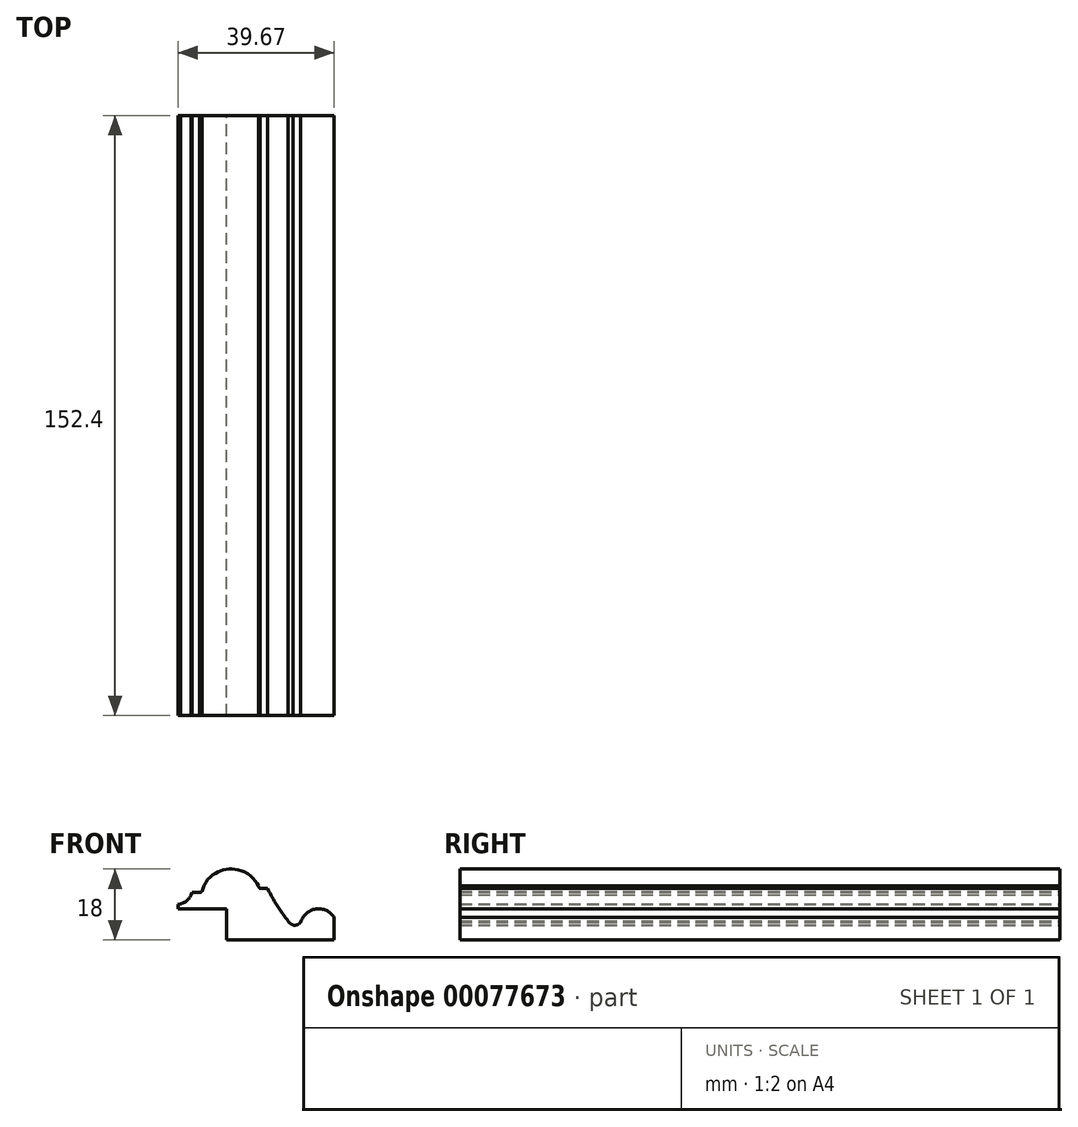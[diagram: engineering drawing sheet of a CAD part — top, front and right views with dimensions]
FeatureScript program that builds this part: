
annotation { "Feature Type Name" : "Feature", "Feature Type Description" : "" }
export const myFeature = defineFeature(function(context is Context, id is Id, definition is map)
    precondition{}
    {
        {
            var Q0;
            Q0=qCreatedBy(makeId("Front.planeOp"),FACE);
            var sketch = newSketch(context, id + "F0", { "sketchPlane" : qUnion([Q0])});
            skLineSegment(sketch, "E0", {"start": v(19.8, -3.3) * mm, "end": v(19.8, -8.99) * mm});
            skLineSegment(sketch, "E1", {"start": v(19.8, -8.99) * mm, "end": v(-7.51, -8.99) * mm});
            skLineSegment(sketch, "E2", {"start": v(-7.51, -8.99) * mm, "end": v(-7.51, -1.08) * mm});
            skLineSegment(sketch, "E3", {"start": v(-7.51, -1.08) * mm, "end": v(-19.86, -1.08) * mm});
            skLineSegment(sketch, "E4", {"start": v(-19.86, -1.08) * mm, "end": v(-19.86, 0) * mm});
            skArc(sketch, "E5", {"start": v(-16.55, 2.43) * mm, "mid": v(-17.63, 0.97) * mm, "end": v(-19.24, 0.14) * mm});
            skArc(sketch, "E6", {"start": v(11.31, -4.54) * mm, "mid": v(15.16, -1.16) * mm, "end": v(19.8, -3.3) * mm});
            skArc(sketch, "E7", {"start": v(11.31, -4.54) * mm, "mid": v(10.68, -5.03) * mm, "end": v(9.9, -5.25) * mm});
            skArc(sketch, "E8", {"start": v(9.9, -5.25) * mm, "mid": v(9.65, -5.26) * mm, "end": v(9.4, -5.24) * mm});
            skArc(sketch, "E9", {"start": v(9.4, -5.24) * mm, "mid": v(8.65, -4.83) * mm, "end": v(8.07, -4.2) * mm});
            skFitSpline(sketch, "E10", {"points": [v(8.07, -4.2) * mm, v(5.46, -0.55) * mm, v(3.74, 2.39) * mm, v(2.9, 4.04) * mm], "startDerivative": vector(-6.87, 9.23) * mm, "endDerivative": vector(-2.98, 6.05) * mm});
            skLineSegment(sketch, "E11", {"start": v(2.9, 4.04) * mm, "end": v(0.99, 4.04) * mm});
            skArc(sketch, "E12", {"start": v(0.99, 4.04) * mm, "mid": v(0.7, 4.33) * mm, "end": v(0.53, 4.7) * mm});
            skArc(sketch, "E13", {"start": v(-13.83, 3.33) * mm, "mid": v(-14.05, 3.12) * mm, "end": v(-14.35, 3.03) * mm});
            skLineSegment(sketch, "E14", {"start": v(-14.35, 3.03) * mm, "end": v(-16.35, 3.03) * mm});
            skLineSegment(sketch, "E15", {"start": v(-16.35, 3.03) * mm, "end": v(-16.55, 2.43) * mm});
            skFitSpline(sketch, "E16", {"points": [v(-13.83, 3.33) * mm, v(-12.94, 5.39) * mm, v(-11.55, 7.11) * mm, v(-9.76, 8.23) * mm, v(-8.4, 8.75) * mm, v(-6.54, 9) * mm, v(-4.7, 8.84) * mm, v(-2.28, 7.88) * mm, v(-0.46, 6.18) * mm, v(0.53, 4.7) * mm], "startDerivative": vector(6.84, 18.17) * mm, "endDerivative": vector(8.8, -13.85) * mm});
            skLineSegment(sketch, "E17", {"start": v(-19.24, 0.14) * mm, "end": v(-19.86, 0) * mm});
            skSolve(sketch);
        }
        {
            var Q0;
            Q0=makeQuery(id+"F0.imprint","IMPRINT",FACE,{"disambiguationData":[TD([[makeQuery(id+"F0.imprint","IMPRINT",EDGE,{"derivedFrom":sQuery(id+"F0.wireOp",EDGE,"E0")}),-1.0]])]});
            extrude(context, id + "F1", {"entities" : qUnion([Q0]), "depth" : 152.4 * mm});
        }
    });
